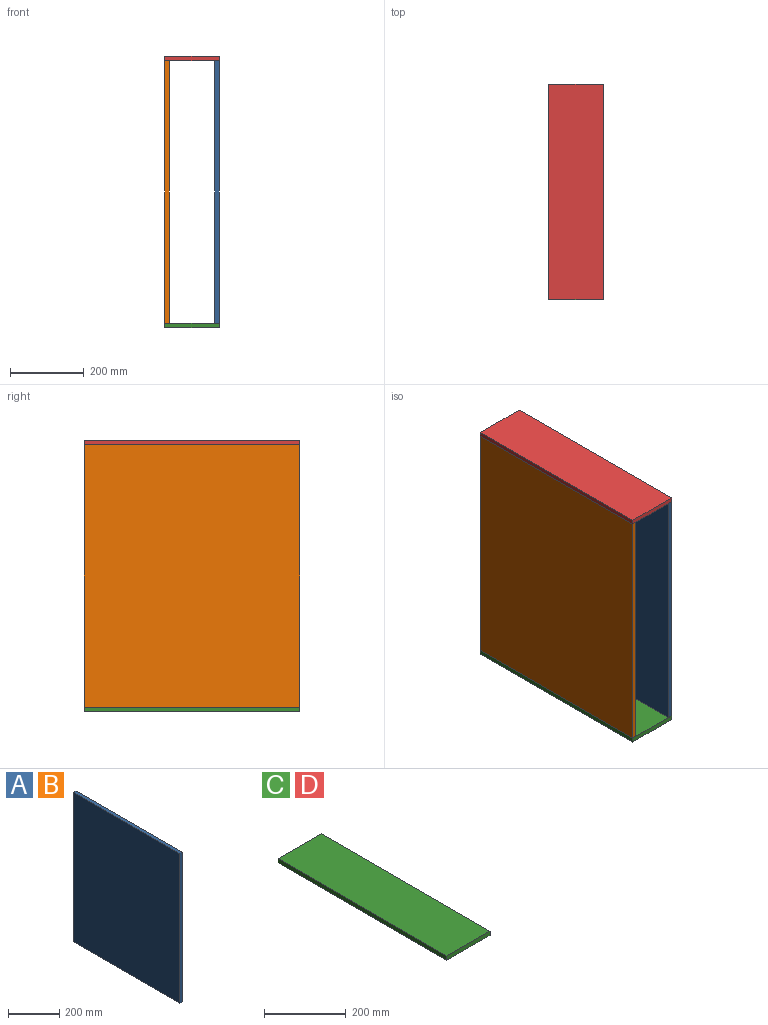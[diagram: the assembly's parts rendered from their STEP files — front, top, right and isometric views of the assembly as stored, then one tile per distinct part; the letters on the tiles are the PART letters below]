
ASSEMBLY  parts=4 mates=1
PART A: 6 faces, bbox 12.7x584.2x711.2 mm
  f0: plane 584.2x12.7mm, normal (0,0,-1), area 7419.3mm2, adj f1,f3,f4,f5
  f1: plane 711.2x12.7mm, normal (0,1,0), area 9032.2mm2, adj f0,f2,f4,f5
  f2: plane 584.2x12.7mm, normal (0,0,1), area 7419.3mm2, adj f1,f3,f4,f5
  f3: plane 711.2x12.7mm, normal (0,-1,0), area 9032.2mm2, adj f0,f2,f4,f5
  f4: plane 711.2x584.2mm, normal (1,0,0), area 415483mm2, adj f0,f1,f2,f3
  f5: plane 711.2x584.2mm, normal (-1,0,0), area 415483mm2, adj f0,f1,f2,f3
PART B: same geometry as A
PART C: 6 faces, bbox 149.2x584.2x12.7 mm
  f0: plane 149.23x12.7mm, normal (0,-1,0), area 1895.2mm2, adj f1,f3,f4,f5
  f1: plane 584.2x12.7mm, normal (1,0,0), area 7419.3mm2, adj f0,f2,f4,f5
  f2: plane 149.23x12.7mm, normal (0,1,0), area 1895.2mm2, adj f1,f3,f4,f5
  f3: plane 584.2x12.7mm, normal (-1,0,0), area 7419.3mm2, adj f0,f2,f4,f5
  f4: plane 584.2x149.23mm, normal (0,0,1), area 87177.2mm2, adj f0,f1,f2,f3
  f5: plane 584.2x149.23mm, normal (0,0,-1), area 87177.2mm2, adj f0,f1,f2,f3
PART D: same geometry as C
PLACE A t=(123.82,0,0)mm
PLACE B t=(-12.7,0,0)mm
PLACE C t=(61.91,0,-368.3)mm
PLACE D t=(61.91,0,355.6)mm
MATE parallel B.f4 <-> A.f4  axis (1,0,0) through (0,0,0)mm
